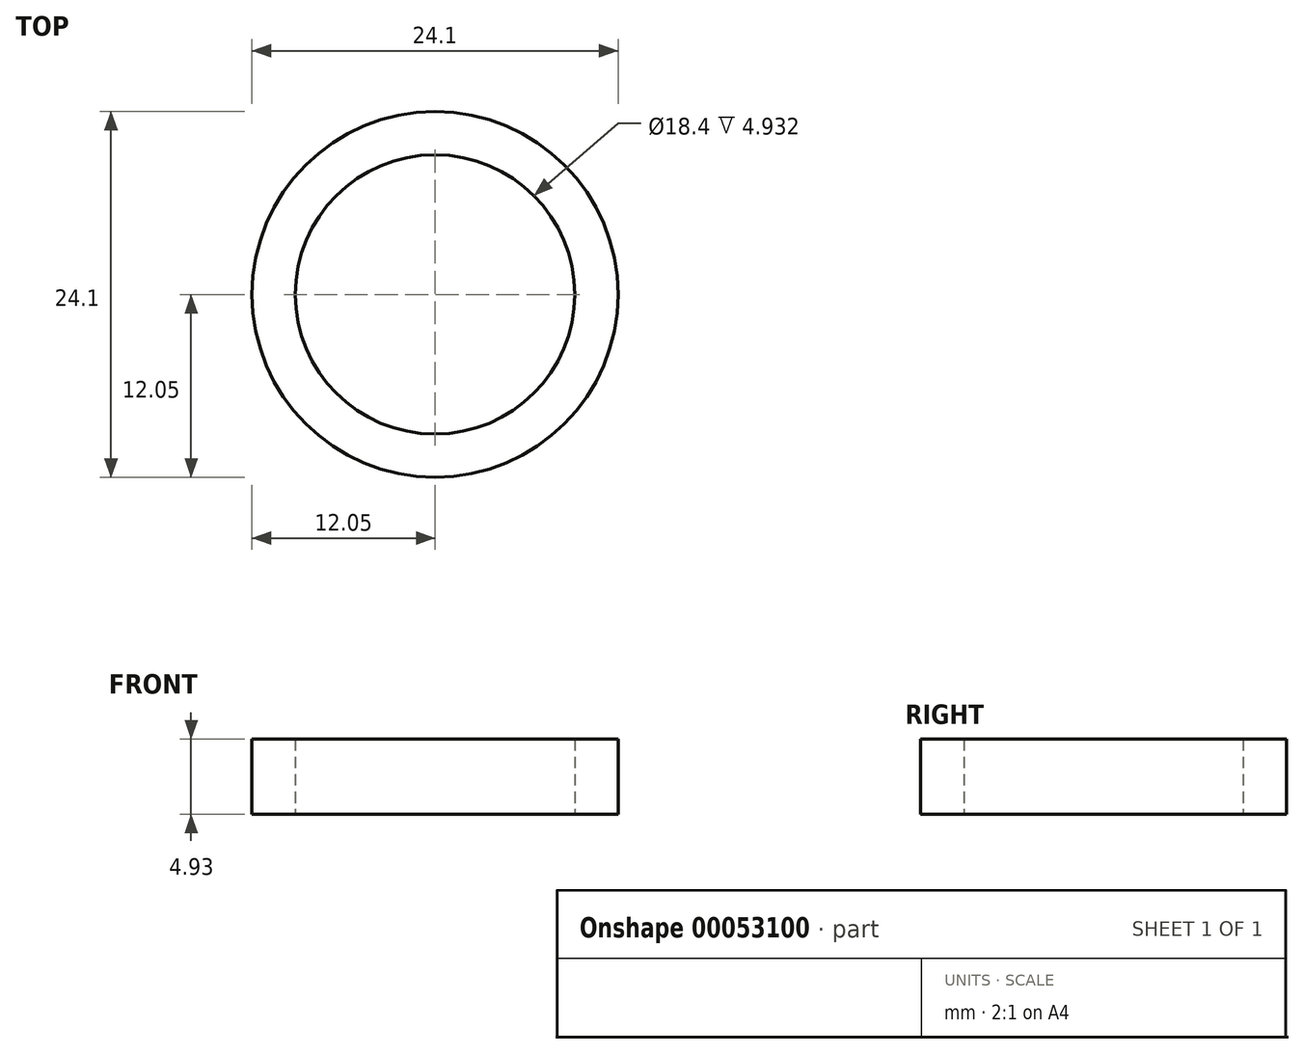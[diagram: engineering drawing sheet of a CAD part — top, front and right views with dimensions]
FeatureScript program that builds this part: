
annotation { "Feature Type Name" : "Feature", "Feature Type Description" : "" }
export const myFeature = defineFeature(function(context is Context, id is Id, definition is map)
    precondition{}
    {
        {
            var Q0;
            Q0=qCreatedBy(makeId("Top.planeOp"),FACE);
            var sketch = newSketch(context, id + "F0", { "sketchPlane" : qUnion([Q0])});
            skCircle(sketch, "E0", {"center": v(0, 0) * mm, "radius": 9.2 * mm});
            skSolve(sketch);
        }
        {
            var Q0;
            Q0=makeQuery(id+"F0.imprint","IMPRINT",FACE,{"disambiguationData":[TD([[makeQuery(id+"F0.imprint","IMPRINT",EDGE,{"derivedFrom":sQuery(id+"F0.wireOp",EDGE,"E0")}),1.0]])]});
            var sketch = newSketch(context, id + "F1", { "sketchPlane" : qUnion([Q0])});
            skCircle(sketch, "E1", {"center": v(0, 0) * mm, "radius": 12.05 * mm});
            skSolve(sketch);
        }
        {
            var Q0;
            Q0=makeQuery(id+"F1.imprint","IMPRINT",FACE,{"disambiguationData":[TD([[makeQuery(id+"F1.imprint","IMPRINT",EDGE,{"derivedFrom":sQuery(id+"F1.wireOp",EDGE,"E1")}),1.0]])]});
            extrude(context, id + "F2", {"entities" : qUnion([Q0]), "depth" : 4.93 * mm});
        }
    });
